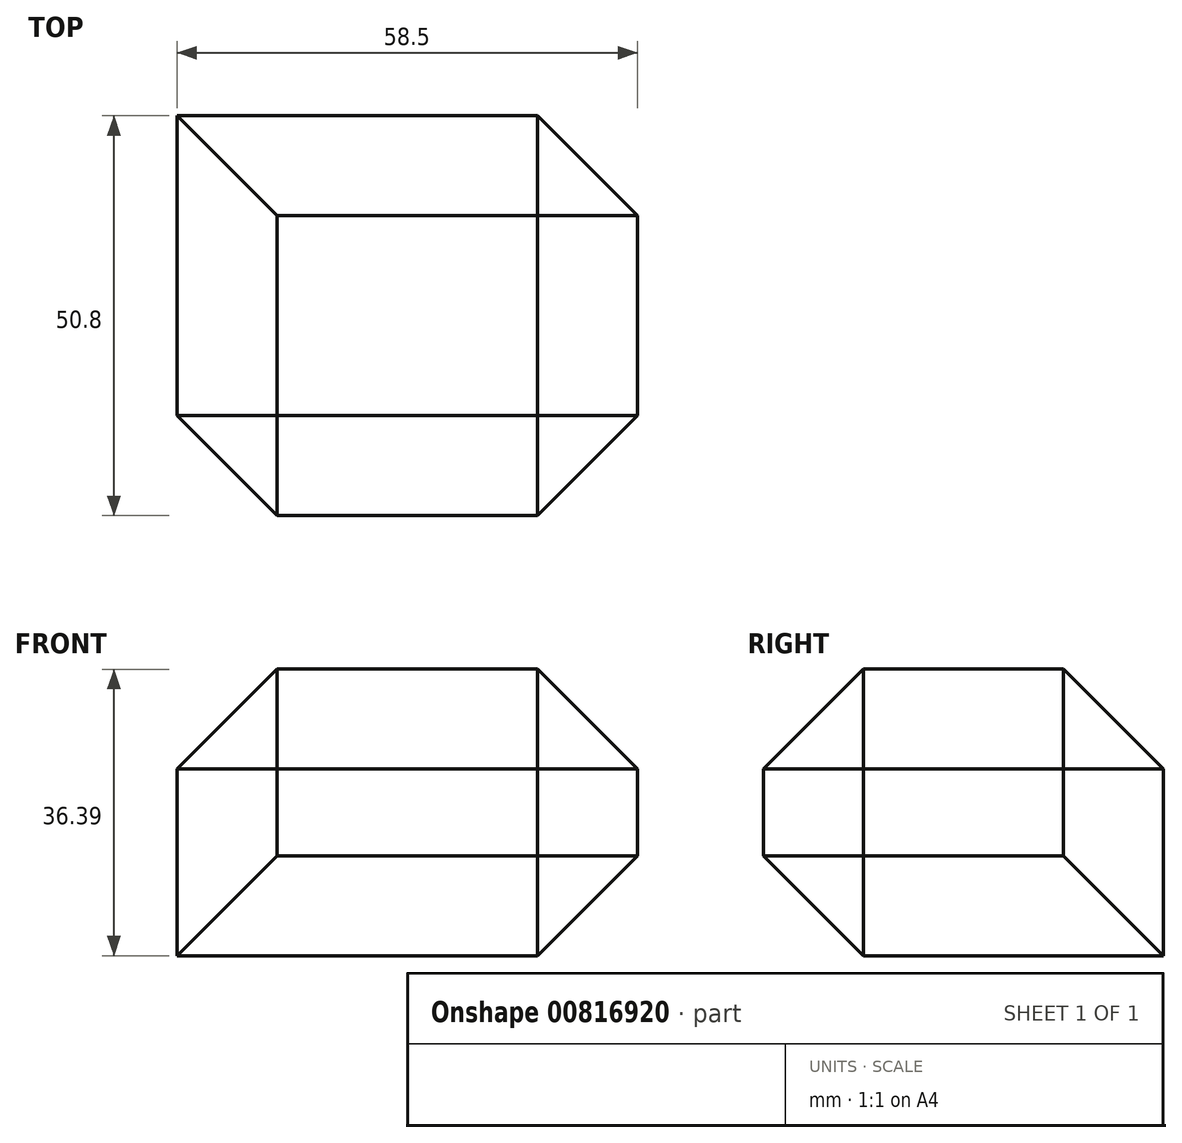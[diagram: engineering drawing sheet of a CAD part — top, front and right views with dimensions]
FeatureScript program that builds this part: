
annotation { "Feature Type Name" : "Feature", "Feature Type Description" : "" }
export const myFeature = defineFeature(function(context is Context, id is Id, definition is map)
    precondition{}
    {
        {
            var Q0;
            Q0=qCreatedBy(makeId("Front.planeOp"),FACE);
            var sketch = newSketch(context, id + "F0", { "sketchPlane" : qUnion([Q0])});
            skLineSegment(sketch, "E0.bottom", {"start": v(-76.57, 23.78) * mm, "end": v(-18.07, 23.78) * mm});
            skLineSegment(sketch, "E0.top", {"start": v(-76.57, 60.17) * mm, "end": v(-18.07, 60.17) * mm});
            skLineSegment(sketch, "E0.left", {"start": v(-76.57, 23.78) * mm, "end": v(-76.57, 60.17) * mm});
            skLineSegment(sketch, "E0.right", {"start": v(-18.07, 23.78) * mm, "end": v(-18.07, 60.17) * mm});
            skSolve(sketch);
        }
        {
            var Q0;
            Q0=makeQuery(id+"F0.imprint","IMPRINT",FACE,{"disambiguationData":[TD([[makeQuery(id+"F0.imprint","IMPRINT",EDGE,{"derivedFrom":sQuery(id+"F0.wireOp",EDGE,"E0.bottom")}),1.0]])]});
            extrude(context, id + "F1", {"entities" : qUnion([Q0]), "depth" : 50.8 * mm, "offsetDistance" : 25.4 * mm});
        }
        {
            var Q0;
            Q0=makeQuery(id+"F1.opExtrude","SWEPT_FACE",FACE,{"disambiguationData":[OSD([sQuery(id+"F0.wireOp",EDGE,"E0.top")])]});
            var Q1;
            Q1=makeQuery(id+"F1.opExtrude","CAP_FACE",FACE,{"disambiguationData":[OSD([sQuery(id+"F0.wireOp",EDGE,"E0.bottom"),sQuery(id+"F0.wireOp",EDGE,"E0.top"),sQuery(id+"F0.wireOp",EDGE,"E0.left"),sQuery(id+"F0.wireOp",EDGE,"E0.right")])],"isStart":false});
            var Q2;
            Q2=makeQuery(id+"F1.opExtrude","SWEPT_FACE",FACE,{"disambiguationData":[OSD([sQuery(id+"F0.wireOp",EDGE,"E0.right")])]});
            chamfer(context, id + "F2", {"entities" : qUnion([Q0, Q1, Q2]), "width" : 12.7 * mm, "tangentPropagation" : true});
        }
    });
